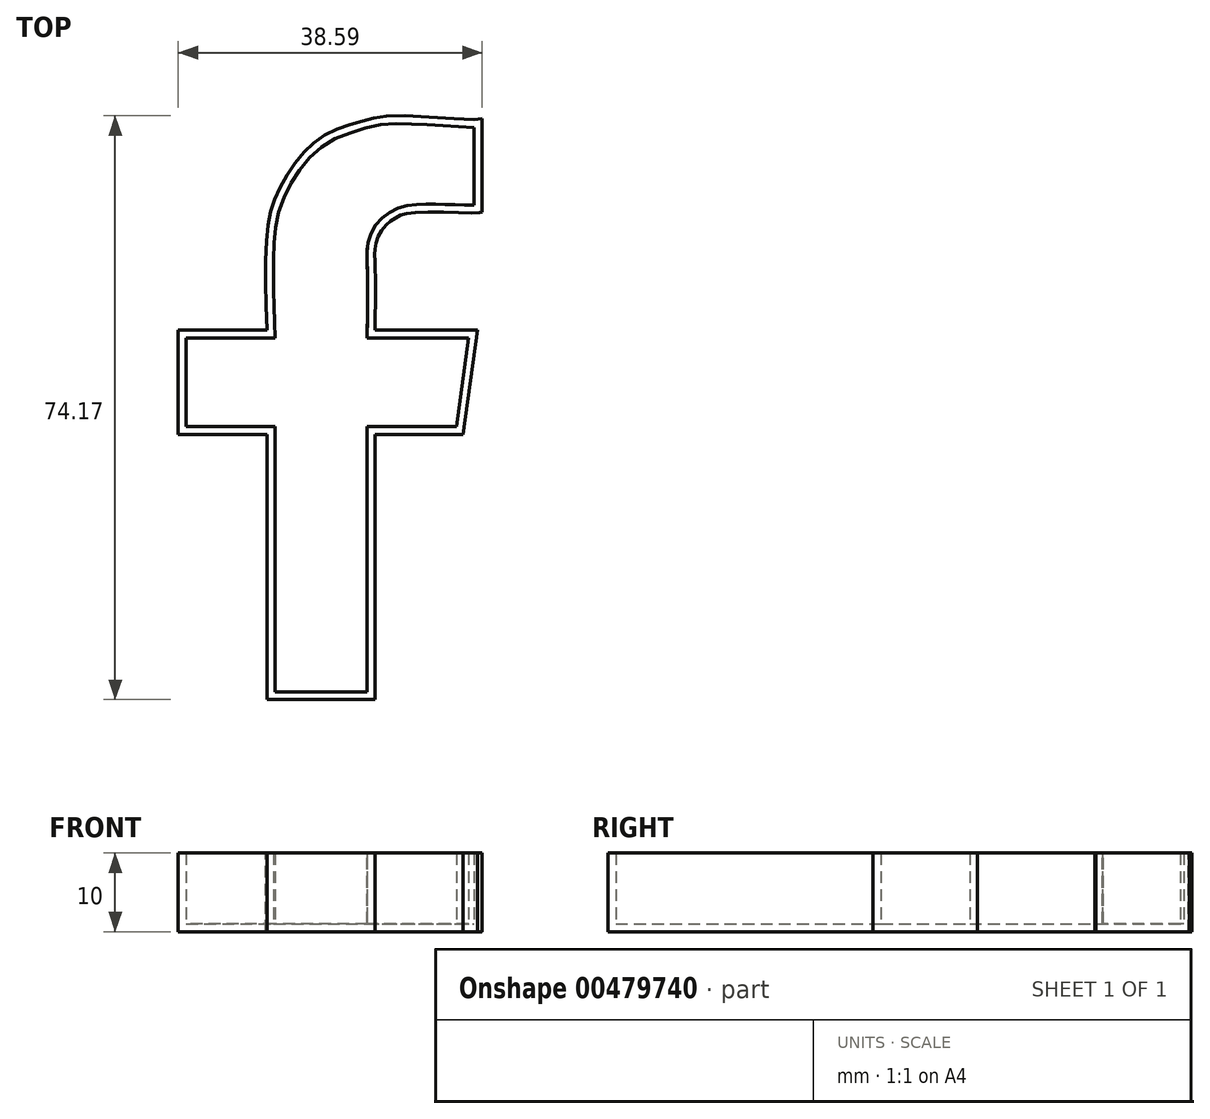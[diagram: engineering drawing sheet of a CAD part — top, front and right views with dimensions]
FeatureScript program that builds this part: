
annotation { "Feature Type Name" : "Feature", "Feature Type Description" : "" }
export const myFeature = defineFeature(function(context is Context, id is Id, definition is map)
    precondition{}
    {
        {
            var Q0;
            Q0=qCreatedBy(makeId("Top.planeOp"),FACE);
            var sketch = newSketch(context, id + "F0", { "sketchPlane" : qUnion([Q0])});
            skLineSegment(sketch, "E0", {"start": v(4, -4.3) * mm, "end": v(4, -37.96) * mm});
            skLineSegment(sketch, "E1", {"start": v(4, -4.3) * mm, "end": v(15.18, -4.3) * mm});
            skLineSegment(sketch, "E2", {"start": v(4, -37.96) * mm, "end": v(-9.74, -37.96) * mm});
            skLineSegment(sketch, "E3", {"start": v(-9.74, -37.96) * mm, "end": v(-9.74, -4.3) * mm});
            skLineSegment(sketch, "E4", {"start": v(-9.74, -4.3) * mm, "end": v(-21.01, -4.3) * mm});
            skLineSegment(sketch, "E5", {"start": v(-21.01, -4.3) * mm, "end": v(-21.01, 9) * mm});
            skLineSegment(sketch, "E6", {"start": v(-21.01, 9) * mm, "end": v(-9.74, 9) * mm});
            skLineSegment(sketch, "E7", {"start": v(15.18, -4.3) * mm, "end": v(16.99, 9) * mm});
            skLineSegment(sketch, "E8", {"start": v(16.99, 9) * mm, "end": v(4, 9) * mm});
            skFitSpline(sketch, "E9", {"points": [v(4, 9) * mm, v(4, 17.15) * mm, v(4, 19.4) * mm, v(4.87, 21.74) * mm, v(6.58, 23.22) * mm, v(9, 23.92) * mm, v(17.47, 23.92) * mm, v(17.55, 24) * mm], "startDerivative": vector(0.42, 40.84) * mm, "endDerivative": vector(0.56, 3.14) * mm});
            skFitSpline(sketch, "E10", {"points": [v(-9.74, 9) * mm, v(-9.74, 21.35) * mm, v(-8.6, 26.02) * mm, v(-5.87, 30.61) * mm, v(-2.29, 33.8) * mm, v(2.22, 35.51) * mm, v(6.97, 36.21) * mm, v(17.55, 35.82) * mm, v(17.55, 35.98) * mm], "startDerivative": vector(-2.22, 72.28) * mm, "endDerivative": vector(-4.12, 7.92) * mm});
            skLineSegment(sketch, "E11", {"start": v(17.58, 35.92) * mm, "end": v(17.55, 24) * mm});
            skSolve(sketch);
        }
        {
            var Q0;
            Q0=makeQuery(id+"F0.imprint","IMPRINT",FACE,{"disambiguationData":[TD([[makeQuery(id+"F0.imprint","IMPRINT",EDGE,{"derivedFrom":sQuery(id+"F0.wireOp",EDGE,"E0")}),-1.0]])]});
            extrude(context, id + "F1", {"entities" : qUnion([Q0]), "depth" : 10 * mm});
        }
        {
            var Q0;
            Q0=makeQuery(id+"F1.opExtrude","CAP_FACE",FACE,{"disambiguationData":[OSD([sQuery(id+"F0.wireOp",EDGE,"E0"),sQuery(id+"F0.wireOp",EDGE,"E1"),sQuery(id+"F0.wireOp",EDGE,"E2"),sQuery(id+"F0.wireOp",EDGE,"E3"),sQuery(id+"F0.wireOp",EDGE,"E4"),sQuery(id+"F0.wireOp",EDGE,"E5"),sQuery(id+"F0.wireOp",EDGE,"E6"),sQuery(id+"F0.wireOp",EDGE,"E7"),sQuery(id+"F0.wireOp",EDGE,"E8"),sQuery(id+"F0.wireOp",EDGE,"E9"),sQuery(id+"F0.wireOp",EDGE,"E10"),sQuery(id+"F0.wireOp",EDGE,"E11")])],"isStart":false});
            shell(context, id + "F2", {"entities" : qUnion([Q0]), "thickness" : 1 * mm});
        }
    });
